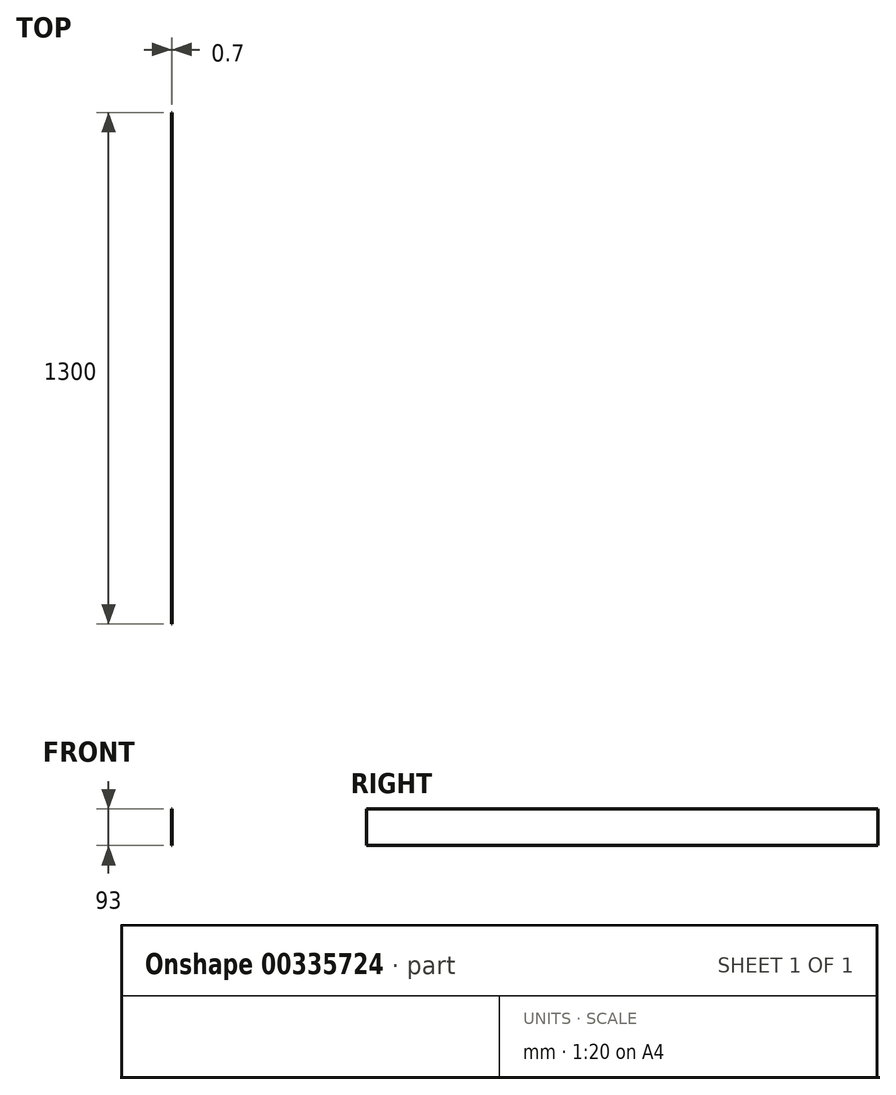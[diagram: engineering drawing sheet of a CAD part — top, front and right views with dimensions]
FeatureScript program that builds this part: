
annotation { "Feature Type Name" : "Feature", "Feature Type Description" : "" }
export const myFeature = defineFeature(function(context is Context, id is Id, definition is map)
    precondition{}
    {
        {
            var Q0;
            Q0=qCreatedBy(makeId("Right.planeOp"),FACE);
            var sketch = newSketch(context, id + "F0", { "sketchPlane" : qUnion([Q0])});
            skLineSegment(sketch, "E0.bottom", {"start": v(0, 0) * mm, "end": v(1300, 0) * mm});
            skLineSegment(sketch, "E0.top", {"start": v(0, 93) * mm, "end": v(1300, 93) * mm});
            skLineSegment(sketch, "E0.left", {"start": v(0, 0) * mm, "end": v(0, 93) * mm});
            skLineSegment(sketch, "E0.right", {"start": v(1300, 0) * mm, "end": v(1300, 93) * mm});
            skSolve(sketch);
        }
        {
            var Q0;
            Q0=makeQuery(id+"F0.imprint","IMPRINT",FACE,{"disambiguationData":[TD([[makeQuery(id+"F0.imprint","IMPRINT",EDGE,{"derivedFrom":sQuery(id+"F0.wireOp",EDGE,"E0.bottom")}),1.0]])]});
            extrude(context, id + "F1", {"entities" : qUnion([Q0]), "depth" : 0.7 * mm, "offsetDistance" : 25 * mm});
        }
    });
